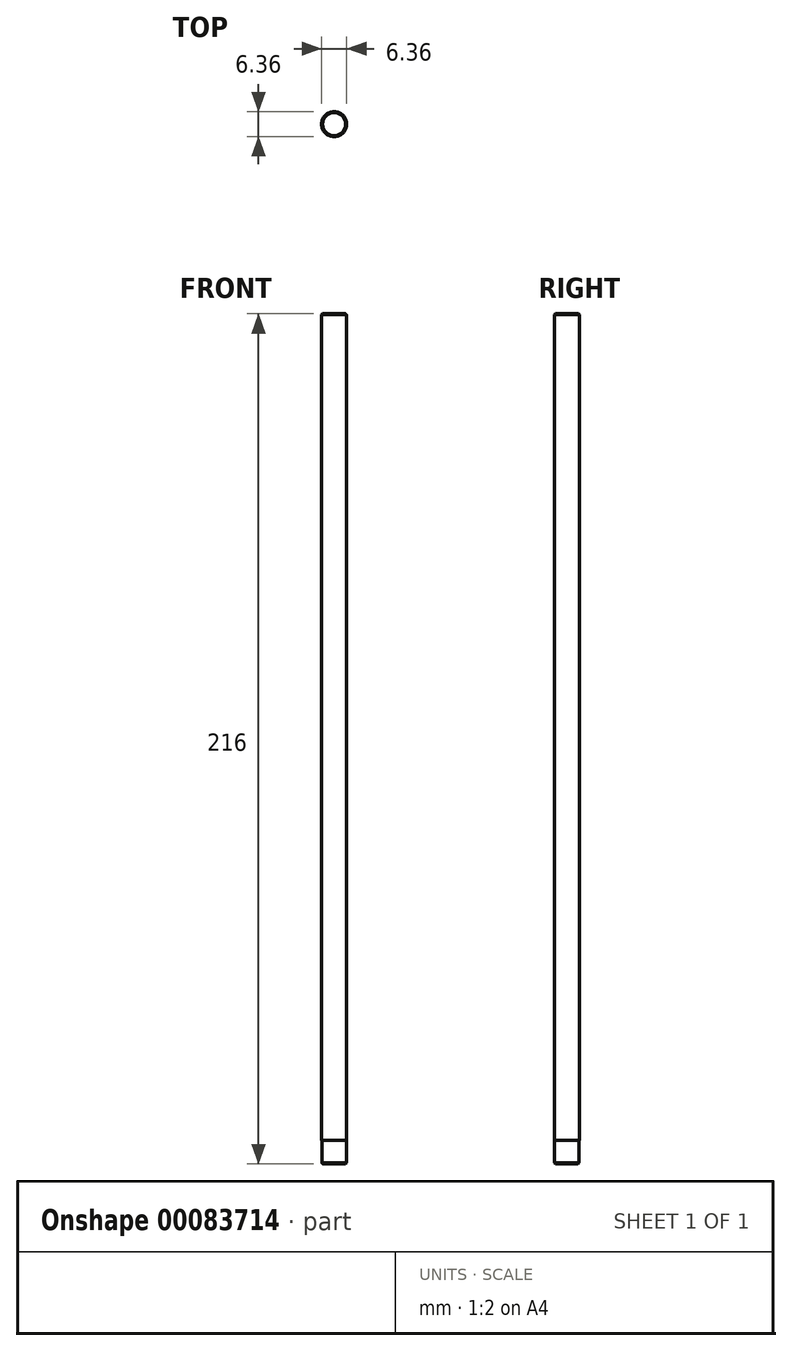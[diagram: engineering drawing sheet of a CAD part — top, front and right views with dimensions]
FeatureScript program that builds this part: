
annotation { "Feature Type Name" : "Feature", "Feature Type Description" : "" }
export const myFeature = defineFeature(function(context is Context, id is Id, definition is map)
    precondition{}
    {
        {
            var Q0;
            Q0=qCreatedBy(makeId("Top.planeOp"),FACE);
            var sketch = newSketch(context, id + "F0", { "sketchPlane" : qUnion([Q0])});
            skCircle(sketch, "E0", {"center": v(0, 0) * mm, "radius": 3.18 * mm});
            skSolve(sketch);
        }
        {
            var Q0;
            Q0=qSketchRegion(id+"F0",true);
            extrude(context, id + "F1", {"entities" : qUnion([Q0]), "oppositeDirection" : true, "depth" : 210 * mm});
        }
        {
            var Q0;
            Q0=makeQuery(id+"F1.opExtrude","CAP_FACE",FACE,{"disambiguationData":[OSD([sQuery(id+"F0.wireOp",EDGE,"E0")])],"isStart":false});
            var sketch = newSketch(context, id + "F2", { "sketchPlane" : qUnion([Q0])});
            skCircle(sketch, "E1", {"center": v(0, 0) * mm, "radius": 3.13 * mm});
            skSolve(sketch);
        }
        {
            var Q0;
            Q0=qSketchRegion(id+"F2",true);
            extrude(context, id + "F3", {"entities" : qUnion([Q0]), "operationType" : NewBodyOperationType.ADD, "depth" : 6 * mm});
        }
        {
            var Q0;
            Q0=makeQuery(id+"F3.opExtrude","CAP_EDGE",EDGE,{"disambiguationData":[OSD([sQuery(id+"F2.wireOp",EDGE,"E1")])],"isStart":false});
            chamfer(context, id + "F4", {"entities" : qUnion([Q0]), "width" : .25 * mm, "tangentPropagation" : true});
        }
        {
            var Q0;
            Q0=makeQuery(id+"F1.opExtrude","CAP_EDGE",EDGE,{"disambiguationData":[OSD([sQuery(id+"F0.wireOp",EDGE,"E0")])],"isStart":true});
            chamfer(context, id + "F5", {"entities" : qUnion([Q0]), "width" : .25 * mm, "tangentPropagation" : true});
        }
    });
